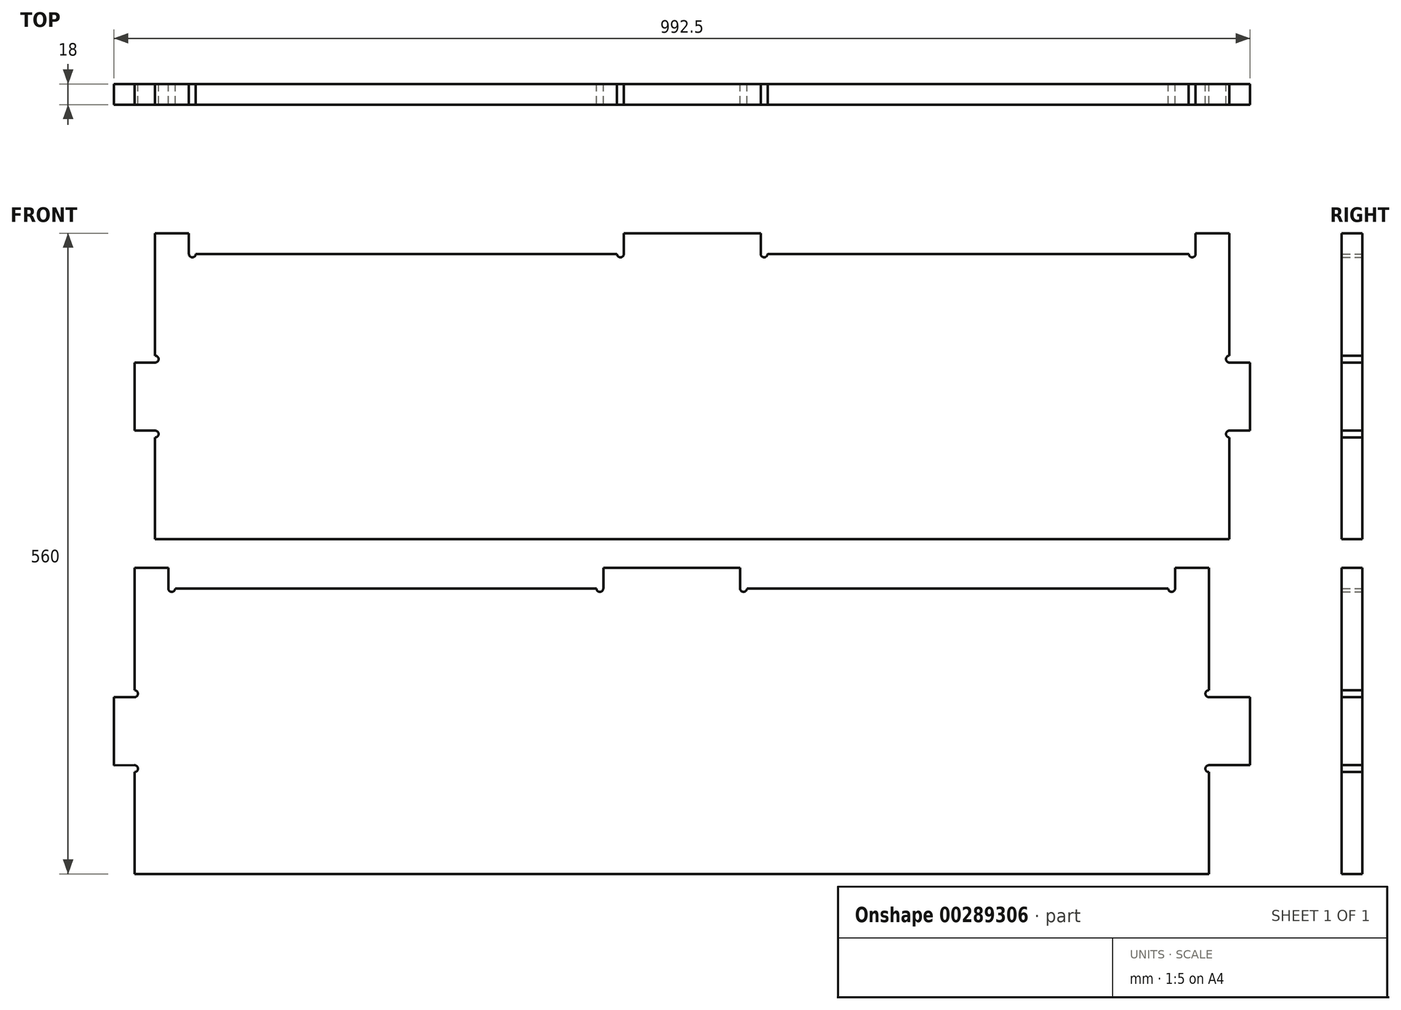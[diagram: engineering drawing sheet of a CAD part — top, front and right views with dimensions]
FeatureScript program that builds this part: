
annotation { "Feature Type Name" : "Feature", "Feature Type Description" : "" }
export const myFeature = defineFeature(function(context is Context, id is Id, definition is map)
    precondition{}
    {
        {
            var Q0;
            Q0=qCreatedBy(makeId("Front.planeOp"),FACE);
            var sketch = newSketch(context, id + "F0", { "sketchPlane" : qUnion([Q0])});
            skLineSegment(sketch, "E0", {"start": v(-600, -1200) * mm, "end": v(600, -1200) * mm});
            skLineSegment(sketch, "E1", {"start": v(600, -1200) * mm, "end": v(600, 1200) * mm});
            skLineSegment(sketch, "E2", {"start": v(600, 1200) * mm, "end": v(-600, 1200) * mm});
            skLineSegment(sketch, "E3", {"start": v(-600, 1200) * mm, "end": v(-600, -1200) * mm});
            skLineSegment(sketch, "E4", {"start": v(-575, -1055.06) * mm, "end": v(-557, -1055) * mm});
            skArc(sketch, "E5", {"start": v(-557, -1055) * mm, "mid": v(-553.99, -1058) * mm, "end": v(-557, -1061.02) * mm});
            skLineSegment(sketch, "E6", {"start": v(-557, -1061.02) * mm, "end": v(-557, -1150) * mm});
            skLineSegment(sketch, "E7", {"start": v(-557, -1150) * mm, "end": v(381.5, -1150) * mm});
            skLineSegment(sketch, "E8", {"start": v(381.5, -1150) * mm, "end": v(381.5, -1061.02) * mm});
            skArc(sketch, "E9", {"start": v(381.5, -1061.02) * mm, "mid": v(378.5, -1058) * mm, "end": v(381.5, -1055) * mm});
            skLineSegment(sketch, "E10", {"start": v(381.5, -1055) * mm, "end": v(417.5, -1055) * mm});
            skLineSegment(sketch, "E11", {"start": v(417.5, -1055) * mm, "end": v(417.5, -995.5) * mm});
            skLineSegment(sketch, "E12", {"start": v(417.5, -995.5) * mm, "end": v(381.5, -995.5) * mm});
            skArc(sketch, "E13", {"start": v(381.5, -995.5) * mm, "mid": v(378.5, -992.49) * mm, "end": v(381.5, -989.48) * mm});
            skLineSegment(sketch, "E14", {"start": v(381.5, -989.48) * mm, "end": v(381.5, -882.5) * mm});
            skLineSegment(sketch, "E15", {"start": v(381.5, -882.5) * mm, "end": v(352, -882.5) * mm});
            skLineSegment(sketch, "E16", {"start": v(352, -882.5) * mm, "end": v(352, -900.5) * mm});
            skArc(sketch, "E17", {"start": v(352, -900.5) * mm, "mid": v(349, -903.5) * mm, "end": v(345.98, -900.5) * mm});
            skLineSegment(sketch, "E18", {"start": v(345.98, -900.5) * mm, "end": v(-21.98, -900.5) * mm});
            skArc(sketch, "E19", {"start": v(-21.98, -900.5) * mm, "mid": v(-24.99, -903.5) * mm, "end": v(-28, -900.5) * mm});
            skLineSegment(sketch, "E20", {"start": v(-28, -900.5) * mm, "end": v(-28, -882.5) * mm});
            skLineSegment(sketch, "E21", {"start": v(-28, -882.5) * mm, "end": v(-147.5, -882.5) * mm});
            skLineSegment(sketch, "E22", {"start": v(-147.5, -882.5) * mm, "end": v(-147.5, -900.5) * mm});
            skArc(sketch, "E23", {"start": v(-147.5, -900.5) * mm, "mid": v(-150.5, -903.5) * mm, "end": v(-153.52, -900.5) * mm});
            skLineSegment(sketch, "E24", {"start": v(-153.52, -900.5) * mm, "end": v(-521.48, -900.5) * mm});
            skArc(sketch, "E25", {"start": v(-521.48, -900.5) * mm, "mid": v(-524.49, -903.5) * mm, "end": v(-527.5, -900.5) * mm});
            skLineSegment(sketch, "E26", {"start": v(-527.5, -900.5) * mm, "end": v(-527.5, -882.5) * mm});
            skLineSegment(sketch, "E27", {"start": v(-527.5, -882.5) * mm, "end": v(-557, -882.5) * mm});
            skLineSegment(sketch, "E28", {"start": v(-557, -882.5) * mm, "end": v(-557, -989.48) * mm});
            skArc(sketch, "E29", {"start": v(-557, -989.48) * mm, "mid": v(-553.99, -992.49) * mm, "end": v(-557, -995.5) * mm});
            skLineSegment(sketch, "E30", {"start": v(-557, -995.5) * mm, "end": v(-575, -995.56) * mm});
            skLineSegment(sketch, "E31", {"start": v(-575, -995.56) * mm, "end": v(-575, -1055.06) * mm});
            skLineSegment(sketch, "E32", {"start": v(-575, -762.56) * mm, "end": v(-557, -762.5) * mm});
            skArc(sketch, "E33", {"start": v(-557, -762.5) * mm, "mid": v(-553.99, -765.5) * mm, "end": v(-557, -768.52) * mm});
            skLineSegment(sketch, "E34", {"start": v(-557, -768.52) * mm, "end": v(-557, -857.5) * mm});
            skLineSegment(sketch, "E35", {"start": v(-557, -857.5) * mm, "end": v(381.5, -857.5) * mm});
            skLineSegment(sketch, "E36", {"start": v(381.5, -857.5) * mm, "end": v(381.5, -768.52) * mm});
            skArc(sketch, "E37", {"start": v(381.5, -768.52) * mm, "mid": v(378.5, -765.5) * mm, "end": v(381.5, -762.5) * mm});
            skLineSegment(sketch, "E38", {"start": v(381.5, -762.5) * mm, "end": v(417.5, -762.5) * mm});
            skLineSegment(sketch, "E39", {"start": v(417.5, -762.5) * mm, "end": v(417.5, -703) * mm});
            skLineSegment(sketch, "E40", {"start": v(417.5, -703) * mm, "end": v(381.5, -703) * mm});
            skArc(sketch, "E41", {"start": v(381.5, -703) * mm, "mid": v(378.5, -699.99) * mm, "end": v(381.5, -696.98) * mm});
            skLineSegment(sketch, "E42", {"start": v(381.5, -696.98) * mm, "end": v(381.5, -590) * mm});
            skLineSegment(sketch, "E43", {"start": v(381.5, -590) * mm, "end": v(352, -590) * mm});
            skLineSegment(sketch, "E44", {"start": v(352, -590) * mm, "end": v(352, -608) * mm});
            skArc(sketch, "E45", {"start": v(352, -608) * mm, "mid": v(349, -611) * mm, "end": v(345.98, -608) * mm});
            skLineSegment(sketch, "E46", {"start": v(345.98, -608) * mm, "end": v(-21.98, -608) * mm});
            skArc(sketch, "E47", {"start": v(-21.98, -608) * mm, "mid": v(-24.99, -611) * mm, "end": v(-28, -608) * mm});
            skLineSegment(sketch, "E48", {"start": v(-28, -608) * mm, "end": v(-28, -590) * mm});
            skLineSegment(sketch, "E49", {"start": v(-28, -590) * mm, "end": v(-147.5, -590) * mm});
            skLineSegment(sketch, "E50", {"start": v(-147.5, -590) * mm, "end": v(-147.5, -608) * mm});
            skArc(sketch, "E51", {"start": v(-147.5, -608) * mm, "mid": v(-150.5, -611) * mm, "end": v(-153.52, -608) * mm});
            skLineSegment(sketch, "E52", {"start": v(-153.52, -608) * mm, "end": v(-521.48, -608) * mm});
            skArc(sketch, "E53", {"start": v(-521.48, -608) * mm, "mid": v(-524.49, -611) * mm, "end": v(-527.5, -608) * mm});
            skLineSegment(sketch, "E54", {"start": v(-527.5, -608) * mm, "end": v(-527.5, -590) * mm});
            skLineSegment(sketch, "E55", {"start": v(-527.5, -590) * mm, "end": v(-557, -590) * mm});
            skLineSegment(sketch, "E56", {"start": v(-557, -590) * mm, "end": v(-557, -696.98) * mm});
            skArc(sketch, "E57", {"start": v(-557, -696.98) * mm, "mid": v(-553.99, -699.99) * mm, "end": v(-557, -703) * mm});
            skLineSegment(sketch, "E58", {"start": v(-557, -703) * mm, "end": v(-575, -703.06) * mm});
            skLineSegment(sketch, "E59", {"start": v(-575, -703.06) * mm, "end": v(-575, -762.56) * mm});
            skLineSegment(sketch, "E60", {"start": v(-575, -470.06) * mm, "end": v(-557, -470) * mm});
            skArc(sketch, "E61", {"start": v(-557, -470) * mm, "mid": v(-553.99, -473) * mm, "end": v(-557, -476.02) * mm});
            skLineSegment(sketch, "E62", {"start": v(-557, -476.02) * mm, "end": v(-557, -565) * mm});
            skLineSegment(sketch, "E63", {"start": v(-557, -565) * mm, "end": v(381.5, -565) * mm});
            skLineSegment(sketch, "E64", {"start": v(381.5, -565) * mm, "end": v(381.5, -476.02) * mm});
            skArc(sketch, "E65", {"start": v(381.5, -476.02) * mm, "mid": v(378.5, -473) * mm, "end": v(381.5, -470) * mm});
            skLineSegment(sketch, "E66", {"start": v(381.5, -470) * mm, "end": v(417.5, -470) * mm});
            skLineSegment(sketch, "E67", {"start": v(417.5, -470) * mm, "end": v(417.5, -410.5) * mm});
            skLineSegment(sketch, "E68", {"start": v(417.5, -410.5) * mm, "end": v(381.5, -410.5) * mm});
            skArc(sketch, "E69", {"start": v(381.5, -410.5) * mm, "mid": v(378.5, -407.49) * mm, "end": v(381.5, -404.48) * mm});
            skLineSegment(sketch, "E70", {"start": v(381.5, -404.48) * mm, "end": v(381.5, -297.5) * mm});
            skLineSegment(sketch, "E71", {"start": v(381.5, -297.5) * mm, "end": v(352, -297.5) * mm});
            skLineSegment(sketch, "E72", {"start": v(352, -297.5) * mm, "end": v(352, -315.5) * mm});
            skArc(sketch, "E73", {"start": v(352, -315.5) * mm, "mid": v(349, -318.5) * mm, "end": v(345.98, -315.5) * mm});
            skLineSegment(sketch, "E74", {"start": v(345.98, -315.5) * mm, "end": v(-21.98, -315.5) * mm});
            skArc(sketch, "E75", {"start": v(-21.98, -315.5) * mm, "mid": v(-24.99, -318.5) * mm, "end": v(-28, -315.5) * mm});
            skLineSegment(sketch, "E76", {"start": v(-28, -315.5) * mm, "end": v(-28, -297.5) * mm});
            skLineSegment(sketch, "E77", {"start": v(-28, -297.5) * mm, "end": v(-147.5, -297.5) * mm});
            skLineSegment(sketch, "E78", {"start": v(-147.5, -297.5) * mm, "end": v(-147.5, -315.5) * mm});
            skArc(sketch, "E79", {"start": v(-147.5, -315.5) * mm, "mid": v(-150.5, -318.5) * mm, "end": v(-153.52, -315.5) * mm});
            skLineSegment(sketch, "E80", {"start": v(-153.52, -315.5) * mm, "end": v(-521.48, -315.5) * mm});
            skArc(sketch, "E81", {"start": v(-521.48, -315.5) * mm, "mid": v(-524.49, -318.5) * mm, "end": v(-527.5, -315.5) * mm});
            skLineSegment(sketch, "E82", {"start": v(-527.5, -315.5) * mm, "end": v(-527.5, -297.5) * mm});
            skLineSegment(sketch, "E83", {"start": v(-527.5, -297.5) * mm, "end": v(-557, -297.5) * mm});
            skLineSegment(sketch, "E84", {"start": v(-557, -297.5) * mm, "end": v(-557, -404.48) * mm});
            skArc(sketch, "E85", {"start": v(-557, -404.48) * mm, "mid": v(-553.99, -407.49) * mm, "end": v(-557, -410.5) * mm});
            skLineSegment(sketch, "E86", {"start": v(-557, -410.5) * mm, "end": v(-575, -410.56) * mm});
            skLineSegment(sketch, "E87", {"start": v(-575, -410.56) * mm, "end": v(-575, -470.06) * mm});
            skLineSegment(sketch, "E88", {"start": v(-575, -177.56) * mm, "end": v(-557, -177.5) * mm});
            skArc(sketch, "E89", {"start": v(-557, -177.5) * mm, "mid": v(-553.99, -180.5) * mm, "end": v(-557, -183.52) * mm});
            skLineSegment(sketch, "E90", {"start": v(-557, -183.52) * mm, "end": v(-557, -272.5) * mm});
            skLineSegment(sketch, "E91", {"start": v(-557, -272.5) * mm, "end": v(381.5, -272.5) * mm});
            skLineSegment(sketch, "E92", {"start": v(381.5, -272.5) * mm, "end": v(381.5, -183.52) * mm});
            skArc(sketch, "E93", {"start": v(381.5, -183.52) * mm, "mid": v(378.5, -180.5) * mm, "end": v(381.5, -177.5) * mm});
            skLineSegment(sketch, "E94", {"start": v(381.5, -177.5) * mm, "end": v(417.5, -177.5) * mm});
            skLineSegment(sketch, "E95", {"start": v(417.5, -177.5) * mm, "end": v(417.5, -118) * mm});
            skLineSegment(sketch, "E96", {"start": v(417.5, -118) * mm, "end": v(381.5, -118) * mm});
            skArc(sketch, "E97", {"start": v(381.5, -118) * mm, "mid": v(378.5, -114.99) * mm, "end": v(381.5, -111.98) * mm});
            skLineSegment(sketch, "E98", {"start": v(381.5, -111.98) * mm, "end": v(381.5, -5) * mm});
            skLineSegment(sketch, "E99", {"start": v(381.5, -5) * mm, "end": v(352, -5) * mm});
            skLineSegment(sketch, "E100", {"start": v(352, -5) * mm, "end": v(352, -23) * mm});
            skArc(sketch, "E101", {"start": v(352, -23) * mm, "mid": v(349, -26) * mm, "end": v(345.98, -23) * mm});
            skLineSegment(sketch, "E102", {"start": v(345.98, -23) * mm, "end": v(-21.98, -23) * mm});
            skArc(sketch, "E103", {"start": v(-21.98, -23) * mm, "mid": v(-24.99, -26) * mm, "end": v(-28, -23) * mm});
            skLineSegment(sketch, "E104", {"start": v(-28, -23) * mm, "end": v(-28, -5) * mm});
            skLineSegment(sketch, "E105", {"start": v(-28, -5) * mm, "end": v(-147.5, -5) * mm});
            skLineSegment(sketch, "E106", {"start": v(-147.5, -5) * mm, "end": v(-147.5, -23) * mm});
            skArc(sketch, "E107", {"start": v(-147.5, -23) * mm, "mid": v(-150.5, -26) * mm, "end": v(-153.52, -23) * mm});
            skLineSegment(sketch, "E108", {"start": v(-153.52, -23) * mm, "end": v(-521.48, -23) * mm});
            skArc(sketch, "E109", {"start": v(-521.48, -23) * mm, "mid": v(-524.49, -26) * mm, "end": v(-527.5, -23) * mm});
            skLineSegment(sketch, "E110", {"start": v(-527.5, -23) * mm, "end": v(-527.5, -5) * mm});
            skLineSegment(sketch, "E111", {"start": v(-527.5, -5) * mm, "end": v(-557, -5) * mm});
            skLineSegment(sketch, "E112", {"start": v(-557, -5) * mm, "end": v(-557, -111.98) * mm});
            skArc(sketch, "E113", {"start": v(-557, -111.98) * mm, "mid": v(-553.99, -114.99) * mm, "end": v(-557, -118) * mm});
            skLineSegment(sketch, "E114", {"start": v(-557, -118) * mm, "end": v(-575, -118.06) * mm});
            skLineSegment(sketch, "E115", {"start": v(-575, -118.06) * mm, "end": v(-575, -177.56) * mm});
            skLineSegment(sketch, "E116", {"start": v(-575, 114.94) * mm, "end": v(-557, 115) * mm});
            skArc(sketch, "E117", {"start": v(-557, 115) * mm, "mid": v(-553.99, 112) * mm, "end": v(-557, 108.98) * mm});
            skLineSegment(sketch, "E118", {"start": v(-557, 108.98) * mm, "end": v(-557, 20) * mm});
            skLineSegment(sketch, "E119", {"start": v(-557, 20) * mm, "end": v(381.5, 20) * mm});
            skLineSegment(sketch, "E120", {"start": v(381.5, 20) * mm, "end": v(381.5, 108.98) * mm});
            skArc(sketch, "E121", {"start": v(381.5, 108.98) * mm, "mid": v(378.5, 112) * mm, "end": v(381.5, 115) * mm});
            skLineSegment(sketch, "E122", {"start": v(381.5, 115) * mm, "end": v(417.5, 115) * mm});
            skLineSegment(sketch, "E123", {"start": v(417.5, 115) * mm, "end": v(417.5, 174.5) * mm});
            skLineSegment(sketch, "E124", {"start": v(417.5, 174.5) * mm, "end": v(381.5, 174.5) * mm});
            skArc(sketch, "E125", {"start": v(381.5, 174.5) * mm, "mid": v(378.5, 177.51) * mm, "end": v(381.5, 180.52) * mm});
            skLineSegment(sketch, "E126", {"start": v(381.5, 180.52) * mm, "end": v(381.5, 287.5) * mm});
            skLineSegment(sketch, "E127", {"start": v(381.5, 287.5) * mm, "end": v(352, 287.5) * mm});
            skLineSegment(sketch, "E128", {"start": v(352, 287.5) * mm, "end": v(352, 269.5) * mm});
            skArc(sketch, "E129", {"start": v(352, 269.5) * mm, "mid": v(349, 266.5) * mm, "end": v(345.98, 269.5) * mm});
            skLineSegment(sketch, "E130", {"start": v(345.98, 269.5) * mm, "end": v(-21.98, 269.5) * mm});
            skArc(sketch, "E131", {"start": v(-21.98, 269.5) * mm, "mid": v(-24.99, 266.5) * mm, "end": v(-28, 269.5) * mm});
            skLineSegment(sketch, "E132", {"start": v(-28, 269.5) * mm, "end": v(-28, 287.5) * mm});
            skLineSegment(sketch, "E133", {"start": v(-28, 287.5) * mm, "end": v(-147.5, 287.5) * mm});
            skLineSegment(sketch, "E134", {"start": v(-147.5, 287.5) * mm, "end": v(-147.5, 269.5) * mm});
            skArc(sketch, "E135", {"start": v(-147.5, 269.5) * mm, "mid": v(-150.5, 266.5) * mm, "end": v(-153.52, 269.5) * mm});
            skLineSegment(sketch, "E136", {"start": v(-153.52, 269.5) * mm, "end": v(-521.48, 269.5) * mm});
            skArc(sketch, "E137", {"start": v(-521.48, 269.5) * mm, "mid": v(-524.49, 266.5) * mm, "end": v(-527.5, 269.5) * mm});
            skLineSegment(sketch, "E138", {"start": v(-527.5, 269.5) * mm, "end": v(-527.5, 287.5) * mm});
            skLineSegment(sketch, "E139", {"start": v(-527.5, 287.5) * mm, "end": v(-557, 287.5) * mm});
            skLineSegment(sketch, "E140", {"start": v(-557, 287.5) * mm, "end": v(-557, 180.52) * mm});
            skArc(sketch, "E141", {"start": v(-557, 180.52) * mm, "mid": v(-553.99, 177.51) * mm, "end": v(-557, 174.5) * mm});
            skLineSegment(sketch, "E142", {"start": v(-557, 174.5) * mm, "end": v(-575, 174.44) * mm});
            skLineSegment(sketch, "E143", {"start": v(-575, 174.44) * mm, "end": v(-575, 114.94) * mm});
            skLineSegment(sketch, "E144", {"start": v(-575, 407.44) * mm, "end": v(-557, 407.5) * mm});
            skArc(sketch, "E145", {"start": v(-557, 407.5) * mm, "mid": v(-553.99, 404.5) * mm, "end": v(-557, 401.48) * mm});
            skLineSegment(sketch, "E146", {"start": v(-557, 401.48) * mm, "end": v(-557, 312.5) * mm});
            skLineSegment(sketch, "E147", {"start": v(-557, 312.5) * mm, "end": v(381.5, 312.5) * mm});
            skLineSegment(sketch, "E148", {"start": v(381.5, 312.5) * mm, "end": v(381.5, 401.48) * mm});
            skArc(sketch, "E149", {"start": v(381.5, 401.48) * mm, "mid": v(378.5, 404.5) * mm, "end": v(381.5, 407.5) * mm});
            skLineSegment(sketch, "E150", {"start": v(381.5, 407.5) * mm, "end": v(417.5, 407.5) * mm});
            skLineSegment(sketch, "E151", {"start": v(417.5, 407.5) * mm, "end": v(417.5, 467) * mm});
            skLineSegment(sketch, "E152", {"start": v(417.5, 467) * mm, "end": v(381.5, 467) * mm});
            skArc(sketch, "E153", {"start": v(381.5, 467) * mm, "mid": v(378.5, 470.01) * mm, "end": v(381.5, 473.02) * mm});
            skLineSegment(sketch, "E154", {"start": v(381.5, 473.02) * mm, "end": v(381.5, 580) * mm});
            skLineSegment(sketch, "E155", {"start": v(381.5, 580) * mm, "end": v(352, 580) * mm});
            skLineSegment(sketch, "E156", {"start": v(352, 580) * mm, "end": v(352, 562) * mm});
            skArc(sketch, "E157", {"start": v(352, 562) * mm, "mid": v(349, 559) * mm, "end": v(345.98, 562) * mm});
            skLineSegment(sketch, "E158", {"start": v(345.98, 562) * mm, "end": v(-21.98, 562) * mm});
            skArc(sketch, "E159", {"start": v(-21.98, 562) * mm, "mid": v(-24.99, 559) * mm, "end": v(-28, 562) * mm});
            skLineSegment(sketch, "E160", {"start": v(-28, 562) * mm, "end": v(-28, 580) * mm});
            skLineSegment(sketch, "E161", {"start": v(-28, 580) * mm, "end": v(-147.5, 580) * mm});
            skLineSegment(sketch, "E162", {"start": v(-147.5, 580) * mm, "end": v(-147.5, 562) * mm});
            skArc(sketch, "E163", {"start": v(-147.5, 562) * mm, "mid": v(-150.5, 559) * mm, "end": v(-153.52, 562) * mm});
            skLineSegment(sketch, "E164", {"start": v(-153.52, 562) * mm, "end": v(-521.48, 562) * mm});
            skArc(sketch, "E165", {"start": v(-521.48, 562) * mm, "mid": v(-524.49, 559) * mm, "end": v(-527.5, 562) * mm});
            skLineSegment(sketch, "E166", {"start": v(-527.5, 562) * mm, "end": v(-527.5, 580) * mm});
            skLineSegment(sketch, "E167", {"start": v(-527.5, 580) * mm, "end": v(-557, 580) * mm});
            skLineSegment(sketch, "E168", {"start": v(-557, 580) * mm, "end": v(-557, 473.02) * mm});
            skArc(sketch, "E169", {"start": v(-557, 473.02) * mm, "mid": v(-553.99, 470.01) * mm, "end": v(-557, 467) * mm});
            skLineSegment(sketch, "E170", {"start": v(-557, 467) * mm, "end": v(-575, 466.94) * mm});
            skLineSegment(sketch, "E171", {"start": v(-575, 466.94) * mm, "end": v(-575, 407.44) * mm});
            skLineSegment(sketch, "E172", {"start": v(-575, 699.94) * mm, "end": v(-557, 700) * mm});
            skArc(sketch, "E173", {"start": v(-557, 700) * mm, "mid": v(-553.99, 697) * mm, "end": v(-557, 693.98) * mm});
            skLineSegment(sketch, "E174", {"start": v(-557, 693.98) * mm, "end": v(-557, 605) * mm});
            skLineSegment(sketch, "E175", {"start": v(-557, 605) * mm, "end": v(381.5, 605) * mm});
            skLineSegment(sketch, "E176", {"start": v(381.5, 605) * mm, "end": v(381.5, 693.98) * mm});
            skArc(sketch, "E177", {"start": v(381.5, 693.98) * mm, "mid": v(378.5, 697) * mm, "end": v(381.5, 700) * mm});
            skLineSegment(sketch, "E178", {"start": v(381.5, 700) * mm, "end": v(417.5, 700) * mm});
            skLineSegment(sketch, "E179", {"start": v(417.5, 700) * mm, "end": v(417.5, 759.5) * mm});
            skLineSegment(sketch, "E180", {"start": v(417.5, 759.5) * mm, "end": v(381.5, 759.5) * mm});
            skArc(sketch, "E181", {"start": v(381.5, 759.5) * mm, "mid": v(378.5, 762.51) * mm, "end": v(381.5, 765.52) * mm});
            skLineSegment(sketch, "E182", {"start": v(381.5, 765.52) * mm, "end": v(381.5, 872.5) * mm});
            skLineSegment(sketch, "E183", {"start": v(381.5, 872.5) * mm, "end": v(352, 872.5) * mm});
            skLineSegment(sketch, "E184", {"start": v(352, 872.5) * mm, "end": v(352, 854.5) * mm});
            skArc(sketch, "E185", {"start": v(352, 854.5) * mm, "mid": v(349, 851.5) * mm, "end": v(345.98, 854.5) * mm});
            skLineSegment(sketch, "E186", {"start": v(345.98, 854.5) * mm, "end": v(-21.98, 854.5) * mm});
            skArc(sketch, "E187", {"start": v(-21.98, 854.5) * mm, "mid": v(-24.99, 851.5) * mm, "end": v(-28, 854.5) * mm});
            skLineSegment(sketch, "E188", {"start": v(-28, 854.5) * mm, "end": v(-28, 872.5) * mm});
            skLineSegment(sketch, "E189", {"start": v(-28, 872.5) * mm, "end": v(-147.5, 872.5) * mm});
            skLineSegment(sketch, "E190", {"start": v(-147.5, 872.5) * mm, "end": v(-147.5, 854.5) * mm});
            skArc(sketch, "E191", {"start": v(-147.5, 854.5) * mm, "mid": v(-150.5, 851.5) * mm, "end": v(-153.52, 854.5) * mm});
            skLineSegment(sketch, "E192", {"start": v(-153.52, 854.5) * mm, "end": v(-521.48, 854.5) * mm});
            skArc(sketch, "E193", {"start": v(-521.48, 854.5) * mm, "mid": v(-524.49, 851.5) * mm, "end": v(-527.5, 854.5) * mm});
            skLineSegment(sketch, "E194", {"start": v(-527.5, 854.5) * mm, "end": v(-527.5, 872.5) * mm});
            skLineSegment(sketch, "E195", {"start": v(-527.5, 872.5) * mm, "end": v(-557, 872.5) * mm});
            skLineSegment(sketch, "E196", {"start": v(-557, 872.5) * mm, "end": v(-557, 765.52) * mm});
            skArc(sketch, "E197", {"start": v(-557, 765.52) * mm, "mid": v(-553.99, 762.51) * mm, "end": v(-557, 759.5) * mm});
            skLineSegment(sketch, "E198", {"start": v(-557, 759.5) * mm, "end": v(-575, 759.44) * mm});
            skLineSegment(sketch, "E199", {"start": v(-575, 759.44) * mm, "end": v(-575, 699.94) * mm});
            skLineSegment(sketch, "E200", {"start": v(-557, 992.44) * mm, "end": v(-539, 992.5) * mm});
            skArc(sketch, "E201", {"start": v(-539, 992.5) * mm, "mid": v(-535.99, 989.5) * mm, "end": v(-539, 986.48) * mm});
            skLineSegment(sketch, "E202", {"start": v(-539, 986.48) * mm, "end": v(-539, 897.5) * mm});
            skLineSegment(sketch, "E203", {"start": v(-539, 897.5) * mm, "end": v(399.5, 897.5) * mm});
            skLineSegment(sketch, "E204", {"start": v(399.5, 897.5) * mm, "end": v(399.5, 986.48) * mm});
            skArc(sketch, "E205", {"start": v(399.5, 986.48) * mm, "mid": v(396.5, 989.5) * mm, "end": v(399.5, 992.5) * mm});
            skLineSegment(sketch, "E206", {"start": v(399.5, 992.5) * mm, "end": v(417.5, 992.5) * mm});
            skLineSegment(sketch, "E207", {"start": v(417.5, 992.5) * mm, "end": v(417.5, 1052) * mm});
            skLineSegment(sketch, "E208", {"start": v(417.5, 1052) * mm, "end": v(399.5, 1052) * mm});
            skArc(sketch, "E209", {"start": v(399.5, 1052) * mm, "mid": v(396.5, 1055.01) * mm, "end": v(399.5, 1058.02) * mm});
            skLineSegment(sketch, "E210", {"start": v(399.5, 1058.02) * mm, "end": v(399.5, 1165) * mm});
            skLineSegment(sketch, "E211", {"start": v(399.5, 1165) * mm, "end": v(370, 1165) * mm});
            skLineSegment(sketch, "E212", {"start": v(370, 1165) * mm, "end": v(370, 1147) * mm});
            skArc(sketch, "E213", {"start": v(370, 1147) * mm, "mid": v(367, 1144) * mm, "end": v(363.98, 1147) * mm});
            skLineSegment(sketch, "E214", {"start": v(363.98, 1147) * mm, "end": v(-3.98, 1147) * mm});
            skArc(sketch, "E215", {"start": v(-3.98, 1147) * mm, "mid": v(-6.99, 1144) * mm, "end": v(-10, 1147) * mm});
            skLineSegment(sketch, "E216", {"start": v(-10, 1147) * mm, "end": v(-10, 1165) * mm});
            skLineSegment(sketch, "E217", {"start": v(-10, 1165) * mm, "end": v(-129.5, 1165) * mm});
            skLineSegment(sketch, "E218", {"start": v(-129.5, 1165) * mm, "end": v(-129.5, 1147) * mm});
            skArc(sketch, "E219", {"start": v(-129.5, 1147) * mm, "mid": v(-132.5, 1144) * mm, "end": v(-135.52, 1147) * mm});
            skLineSegment(sketch, "E220", {"start": v(-135.52, 1147) * mm, "end": v(-503.48, 1147) * mm});
            skArc(sketch, "E221", {"start": v(-503.48, 1147) * mm, "mid": v(-506.49, 1144) * mm, "end": v(-509.5, 1147) * mm});
            skLineSegment(sketch, "E222", {"start": v(-509.5, 1147) * mm, "end": v(-509.5, 1165) * mm});
            skLineSegment(sketch, "E223", {"start": v(-509.5, 1165) * mm, "end": v(-539, 1165) * mm});
            skLineSegment(sketch, "E224", {"start": v(-539, 1165) * mm, "end": v(-539, 1058.02) * mm});
            skArc(sketch, "E225", {"start": v(-539, 1058.02) * mm, "mid": v(-535.99, 1055.01) * mm, "end": v(-539, 1052) * mm});
            skLineSegment(sketch, "E226", {"start": v(-539, 1052) * mm, "end": v(-557, 1051.94) * mm});
            skLineSegment(sketch, "E227", {"start": v(-557, 1051.94) * mm, "end": v(-557, 992.44) * mm});
            skArc(sketch, "E228", {"start": v(-593.32, 1112.31) * mm, "mid": v(-595.97, 1111.21) * mm, "end": v(-597.07, 1108.56) * mm});
            skArc(sketch, "E229", {"start": v(-597.07, 1108.56) * mm, "mid": v(-595.97, 1105.91) * mm, "end": v(-593.32, 1104.81) * mm});
            skArc(sketch, "E230", {"start": v(-593.32, 1104.81) * mm, "mid": v(-590.67, 1105.91) * mm, "end": v(-589.57, 1108.56) * mm});
            skArc(sketch, "E231", {"start": v(-589.57, 1108.56) * mm, "mid": v(-590.67, 1111.21) * mm, "end": v(-593.32, 1112.31) * mm});
            skArc(sketch, "E232", {"start": v(-590.57, 671.44) * mm, "mid": v(-593.22, 670.34) * mm, "end": v(-594.32, 667.69) * mm});
            skArc(sketch, "E233", {"start": v(-594.32, 667.69) * mm, "mid": v(-593.22, 665.04) * mm, "end": v(-590.57, 663.94) * mm});
            skArc(sketch, "E234", {"start": v(-590.57, 663.94) * mm, "mid": v(-587.92, 665.04) * mm, "end": v(-586.82, 667.69) * mm});
            skArc(sketch, "E235", {"start": v(-586.82, 667.69) * mm, "mid": v(-587.92, 670.34) * mm, "end": v(-590.57, 671.44) * mm});
            skArc(sketch, "E236", {"start": v(-592.5, 84.98) * mm, "mid": v(-595.15, 83.88) * mm, "end": v(-596.24, 81.23) * mm});
            skArc(sketch, "E237", {"start": v(-596.24, 81.23) * mm, "mid": v(-595.15, 78.58) * mm, "end": v(-592.5, 77.48) * mm});
            skArc(sketch, "E238", {"start": v(-592.5, 77.48) * mm, "mid": v(-589.84, 78.58) * mm, "end": v(-588.74, 81.23) * mm});
            skArc(sketch, "E239", {"start": v(-588.74, 81.23) * mm, "mid": v(-589.84, 83.88) * mm, "end": v(-592.5, 84.98) * mm});
            skArc(sketch, "E240", {"start": v(-592.5, -509.16) * mm, "mid": v(-595.15, -510.26) * mm, "end": v(-596.24, -512.91) * mm});
            skArc(sketch, "E241", {"start": v(-596.24, -512.91) * mm, "mid": v(-595.15, -515.57) * mm, "end": v(-592.5, -516.66) * mm});
            skArc(sketch, "E242", {"start": v(-592.5, -516.66) * mm, "mid": v(-589.84, -515.57) * mm, "end": v(-588.74, -512.91) * mm});
            skArc(sketch, "E243", {"start": v(-588.74, -512.91) * mm, "mid": v(-589.84, -510.26) * mm, "end": v(-592.5, -509.16) * mm});
            skArc(sketch, "E244", {"start": v(-590.57, -959.1) * mm, "mid": v(-593.22, -960.2) * mm, "end": v(-594.32, -962.85) * mm});
            skArc(sketch, "E245", {"start": v(-594.32, -962.85) * mm, "mid": v(-593.22, -965.5) * mm, "end": v(-590.57, -966.6) * mm});
            skArc(sketch, "E246", {"start": v(-590.57, -966.6) * mm, "mid": v(-587.92, -965.5) * mm, "end": v(-586.82, -962.85) * mm});
            skArc(sketch, "E247", {"start": v(-586.82, -962.85) * mm, "mid": v(-587.92, -960.2) * mm, "end": v(-590.57, -959.1) * mm});
            skArc(sketch, "E248", {"start": v(-315.6, -1170.13) * mm, "mid": v(-318.26, -1171.23) * mm, "end": v(-319.36, -1173.88) * mm});
            skArc(sketch, "E249", {"start": v(-319.36, -1173.88) * mm, "mid": v(-318.26, -1176.53) * mm, "end": v(-315.6, -1177.63) * mm});
            skArc(sketch, "E250", {"start": v(-315.6, -1177.63) * mm, "mid": v(-312.96, -1176.53) * mm, "end": v(-311.86, -1173.88) * mm});
            skArc(sketch, "E251", {"start": v(-311.86, -1173.88) * mm, "mid": v(-312.96, -1171.23) * mm, "end": v(-315.6, -1170.13) * mm});
            skArc(sketch, "E252", {"start": v(201.14, -1174.94) * mm, "mid": v(198.5, -1176.03) * mm, "end": v(197.4, -1178.69) * mm});
            skArc(sketch, "E253", {"start": v(197.4, -1178.69) * mm, "mid": v(198.5, -1181.34) * mm, "end": v(201.14, -1182.44) * mm});
            skArc(sketch, "E254", {"start": v(201.14, -1182.44) * mm, "mid": v(203.8, -1181.34) * mm, "end": v(204.9, -1178.69) * mm});
            skArc(sketch, "E255", {"start": v(204.9, -1178.69) * mm, "mid": v(203.8, -1176.03) * mm, "end": v(201.14, -1174.94) * mm});
            skArc(sketch, "E256", {"start": v(220.27, 1188.59) * mm, "mid": v(217.62, 1187.49) * mm, "end": v(216.52, 1184.84) * mm});
            skArc(sketch, "E257", {"start": v(216.52, 1184.84) * mm, "mid": v(217.62, 1182.18) * mm, "end": v(220.27, 1181.09) * mm});
            skArc(sketch, "E258", {"start": v(220.27, 1181.09) * mm, "mid": v(222.93, 1182.18) * mm, "end": v(224.02, 1184.84) * mm});
            skArc(sketch, "E259", {"start": v(224.02, 1184.84) * mm, "mid": v(222.93, 1187.49) * mm, "end": v(220.27, 1188.59) * mm});
            skArc(sketch, "E260", {"start": v(-272.95, 1187.6) * mm, "mid": v(-275.6, 1186.5) * mm, "end": v(-276.7, 1183.85) * mm});
            skArc(sketch, "E261", {"start": v(-276.7, 1183.85) * mm, "mid": v(-275.6, 1181.2) * mm, "end": v(-272.95, 1180.1) * mm});
            skArc(sketch, "E262", {"start": v(-272.95, 1180.1) * mm, "mid": v(-270.3, 1181.2) * mm, "end": v(-269.2, 1183.85) * mm});
            skArc(sketch, "E263", {"start": v(-269.2, 1183.85) * mm, "mid": v(-270.3, 1186.5) * mm, "end": v(-272.95, 1187.6) * mm});
            skArc(sketch, "E264", {"start": v(-185.73, 878.8) * mm, "mid": v(-187.85, 877.92) * mm, "end": v(-188.73, 875.8) * mm});
            skArc(sketch, "E265", {"start": v(-188.73, 875.8) * mm, "mid": v(-187.85, 873.68) * mm, "end": v(-185.73, 872.8) * mm});
            skArc(sketch, "E266", {"start": v(-185.73, 872.8) * mm, "mid": v(-183.6, 873.68) * mm, "end": v(-182.73, 875.8) * mm});
            skArc(sketch, "E267", {"start": v(-182.73, 875.8) * mm, "mid": v(-183.6, 877.92) * mm, "end": v(-185.73, 878.8) * mm});
            skArc(sketch, "E268", {"start": v(-1.88, 585.77) * mm, "mid": v(-4, 584.9) * mm, "end": v(-4.88, 582.77) * mm});
            skArc(sketch, "E269", {"start": v(-4.88, 582.77) * mm, "mid": v(-4, 580.65) * mm, "end": v(-1.88, 579.77) * mm});
            skArc(sketch, "E270", {"start": v(-1.88, 579.77) * mm, "mid": v(0.24, 580.65) * mm, "end": v(1.12, 582.77) * mm});
            skArc(sketch, "E271", {"start": v(1.12, 582.77) * mm, "mid": v(0.24, 584.9) * mm, "end": v(-1.88, 585.77) * mm});
            skArc(sketch, "E272", {"start": v(-175.62, 292.53) * mm, "mid": v(-177.74, 291.65) * mm, "end": v(-178.62, 289.53) * mm});
            skArc(sketch, "E273", {"start": v(-178.62, 289.53) * mm, "mid": v(-177.74, 287.41) * mm, "end": v(-175.62, 286.53) * mm});
            skArc(sketch, "E274", {"start": v(-175.62, 286.53) * mm, "mid": v(-173.5, 287.41) * mm, "end": v(-172.62, 289.53) * mm});
            skArc(sketch, "E275", {"start": v(-172.62, 289.53) * mm, "mid": v(-173.5, 291.65) * mm, "end": v(-175.62, 292.53) * mm});
            skArc(sketch, "E276", {"start": v(-3.4, 0.74) * mm, "mid": v(-5.51, -0.14) * mm, "end": v(-6.4, -2.26) * mm});
            skArc(sketch, "E277", {"start": v(-6.4, -2.26) * mm, "mid": v(-5.51, -4.38) * mm, "end": v(-3.4, -5.26) * mm});
            skArc(sketch, "E278", {"start": v(-3.4, -5.26) * mm, "mid": v(-1.27, -4.38) * mm, "end": v(-0.4, -2.26) * mm});
            skArc(sketch, "E279", {"start": v(-0.4, -2.26) * mm, "mid": v(-1.27, -0.14) * mm, "end": v(-3.4, 0.74) * mm});
            skArc(sketch, "E280", {"start": v(-176.7, -292.01) * mm, "mid": v(-178.81, -292.9) * mm, "end": v(-179.7, -295.01) * mm});
            skArc(sketch, "E281", {"start": v(-179.7, -295.01) * mm, "mid": v(-178.81, -297.14) * mm, "end": v(-176.7, -298.01) * mm});
            skArc(sketch, "E282", {"start": v(-176.7, -298.01) * mm, "mid": v(-174.57, -297.14) * mm, "end": v(-173.7, -295.01) * mm});
            skArc(sketch, "E283", {"start": v(-173.7, -295.01) * mm, "mid": v(-174.57, -292.9) * mm, "end": v(-176.7, -292.01) * mm});
            skArc(sketch, "E284", {"start": v(-5.78, -584.08) * mm, "mid": v(-7.9, -584.96) * mm, "end": v(-8.78, -587.08) * mm});
            skArc(sketch, "E285", {"start": v(-8.78, -587.08) * mm, "mid": v(-7.9, -589.2) * mm, "end": v(-5.78, -590.08) * mm});
            skArc(sketch, "E286", {"start": v(-5.78, -590.08) * mm, "mid": v(-3.66, -589.2) * mm, "end": v(-2.78, -587.08) * mm});
            skArc(sketch, "E287", {"start": v(-2.78, -587.08) * mm, "mid": v(-3.66, -584.96) * mm, "end": v(-5.78, -584.08) * mm});
            skArc(sketch, "E288", {"start": v(-176.64, -875.3) * mm, "mid": v(-178.76, -876.17) * mm, "end": v(-179.64, -878.3) * mm});
            skArc(sketch, "E289", {"start": v(-179.64, -878.3) * mm, "mid": v(-178.76, -880.42) * mm, "end": v(-176.64, -881.3) * mm});
            skArc(sketch, "E290", {"start": v(-176.64, -881.3) * mm, "mid": v(-174.52, -880.42) * mm, "end": v(-173.64, -878.3) * mm});
            skArc(sketch, "E291", {"start": v(-173.64, -878.3) * mm, "mid": v(-174.52, -876.17) * mm, "end": v(-176.64, -875.3) * mm});
            skArc(sketch, "E292", {"start": v(407.32, -1077) * mm, "mid": v(405.2, -1077.88) * mm, "end": v(404.32, -1080) * mm});
            skArc(sketch, "E293", {"start": v(404.32, -1080) * mm, "mid": v(405.2, -1082.13) * mm, "end": v(407.32, -1083) * mm});
            skArc(sketch, "E294", {"start": v(407.32, -1083) * mm, "mid": v(409.44, -1082.13) * mm, "end": v(410.32, -1080) * mm});
            skArc(sketch, "E295", {"start": v(410.32, -1080) * mm, "mid": v(409.44, -1077.88) * mm, "end": v(407.32, -1077) * mm});
            skArc(sketch, "E296", {"start": v(413.69, -503.3) * mm, "mid": v(411.57, -504.17) * mm, "end": v(410.69, -506.3) * mm});
            skArc(sketch, "E297", {"start": v(410.69, -506.3) * mm, "mid": v(411.57, -508.41) * mm, "end": v(413.69, -509.3) * mm});
            skArc(sketch, "E298", {"start": v(413.69, -509.3) * mm, "mid": v(415.8, -508.41) * mm, "end": v(416.69, -506.3) * mm});
            skArc(sketch, "E299", {"start": v(416.69, -506.3) * mm, "mid": v(415.8, -504.17) * mm, "end": v(413.69, -503.3) * mm});
            skArc(sketch, "E300", {"start": v(413.69, 81.29) * mm, "mid": v(411.57, 80.41) * mm, "end": v(410.69, 78.29) * mm});
            skArc(sketch, "E301", {"start": v(410.69, 78.29) * mm, "mid": v(411.57, 76.17) * mm, "end": v(413.69, 75.29) * mm});
            skArc(sketch, "E302", {"start": v(413.69, 75.29) * mm, "mid": v(415.8, 76.17) * mm, "end": v(416.69, 78.29) * mm});
            skArc(sketch, "E303", {"start": v(416.69, 78.29) * mm, "mid": v(415.8, 80.41) * mm, "end": v(413.69, 81.29) * mm});
            skArc(sketch, "E304", {"start": v(410.81, 670.18) * mm, "mid": v(408.7, 669.3) * mm, "end": v(407.81, 667.18) * mm});
            skArc(sketch, "E305", {"start": v(407.81, 667.18) * mm, "mid": v(408.7, 665.06) * mm, "end": v(410.81, 664.18) * mm});
            skArc(sketch, "E306", {"start": v(410.81, 664.18) * mm, "mid": v(412.94, 665.06) * mm, "end": v(413.81, 667.18) * mm});
            skArc(sketch, "E307", {"start": v(413.81, 667.18) * mm, "mid": v(412.94, 669.3) * mm, "end": v(410.81, 670.18) * mm});
            skArc(sketch, "E308", {"start": v(410.81, 961.75) * mm, "mid": v(408.7, 960.87) * mm, "end": v(407.81, 958.75) * mm});
            skArc(sketch, "E309", {"start": v(407.81, 958.75) * mm, "mid": v(408.7, 956.63) * mm, "end": v(410.81, 955.75) * mm});
            skArc(sketch, "E310", {"start": v(410.81, 955.75) * mm, "mid": v(412.94, 956.63) * mm, "end": v(413.81, 958.75) * mm});
            skArc(sketch, "E311", {"start": v(413.81, 958.75) * mm, "mid": v(412.94, 960.87) * mm, "end": v(410.81, 961.75) * mm});
            skSolve(sketch);
        }
        {
            var Q0;
            Q0=makeQuery(id+"F0.imprint","IMPRINT",FACE,{"disambiguationData":[TD([[makeQuery(id+"F0.imprint","IMPRINT",EDGE,{"derivedFrom":sQuery(id+"F0.wireOp",EDGE,"E172")}),1.0]])]});
            extrude(context, id + "F1", {"entities" : qUnion([Q0]), "depth" : 18 * mm});
        }
        {
            var Q0;
            Q0=makeQuery(id+"F0.imprint","IMPRINT",FACE,{"disambiguationData":[TD([[makeQuery(id+"F0.imprint","IMPRINT",EDGE,{"derivedFrom":sQuery(id+"F0.wireOp",EDGE,"E200")}),1.0]])]});
            extrude(context, id + "F2", {"entities" : qUnion([Q0]), "depth" : 18 * mm});
        }
    });
